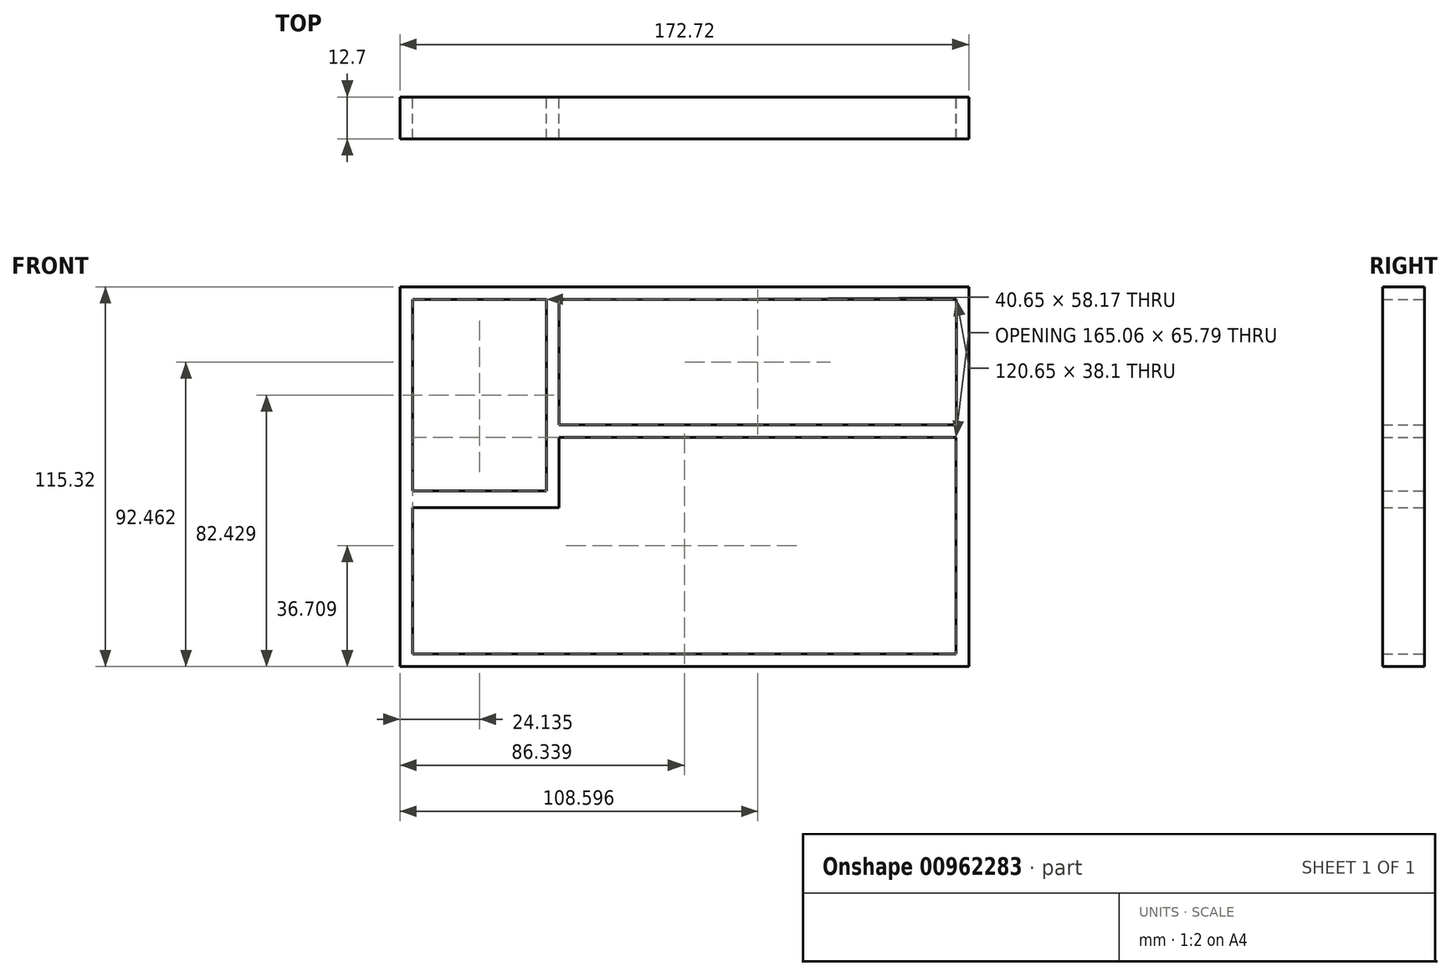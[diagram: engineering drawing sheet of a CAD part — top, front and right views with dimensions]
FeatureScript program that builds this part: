
annotation { "Feature Type Name" : "Feature", "Feature Type Description" : "" }
export const myFeature = defineFeature(function(context is Context, id is Id, definition is map)
    precondition{}
    {
        {
            var Q0;
            Q0=qCreatedBy(makeId("Front.planeOp"),FACE);
            var sketch = newSketch(context, id + "F0", { "sketchPlane" : qUnion([Q0])});
            skLineSegment(sketch, "E0.top", {"start": v(-81.04, -48) * mm, "end": v(84.02, -48) * mm});
            skLineSegment(sketch, "E0.left", {"start": v(-81.04, -3.56) * mm, "end": v(-81.04, -48) * mm});
            skLineSegment(sketch, "E0.right", {"start": v(84.02, -5.13) * mm, "end": v(84.02, -48) * mm});
            skLineSegment(sketch, "E1.top", {"start": v(-84.85, -51.82) * mm, "end": v(87.87, -51.82) * mm});
            skLineSegment(sketch, "E1.right", {"start": v(87.87, 17.78) * mm, "end": v(87.87, -51.82) * mm});
            skLineSegment(sketch, "E2.top", {"start": v(87.87, 63.5) * mm, "end": v(-84.85, 63.5) * mm});
            skLineSegment(sketch, "E2.left", {"start": v(87.87, 17.78) * mm, "end": v(87.87, 63.5) * mm});
            skLineSegment(sketch, "E3.left", {"start": v(-81.04, 1.52) * mm, "end": v(-81.04, 59.7) * mm});
            skLineSegment(sketch, "E3.right", {"start": v(84.07, 21.6) * mm, "end": v(84.07, 59.7) * mm});
            skPoint(sketch, "E4.endSnap0", {"position": v(1.51, 21.6) * mm});
            skLineSegment(sketch, "E5.left", {"start": v(-40.39, 59.7) * mm, "end": v(-40.39, 1.52) * mm});
            skLineSegment(sketch, "E5.right", {"start": v(-36.58, 59.7) * mm, "end": v(-36.58, 21.6) * mm});
            skLineSegment(sketch, "E6", {"start": v(-84.85, 63.5) * mm, "end": v(-84.85, -51.82) * mm});
            skLineSegment(sketch, "E7", {"start": v(-81.04, 1.52) * mm, "end": v(-40.39, 1.52) * mm});
            skLineSegment(sketch, "E8", {"start": v(-81.04, 59.7) * mm, "end": v(-40.39, 59.7) * mm});
            skLineSegment(sketch, "E9", {"start": v(-36.58, 59.7) * mm, "end": v(84.07, 59.7) * mm});
            skLineSegment(sketch, "E10", {"start": v(84.07, 21.6) * mm, "end": v(-36.58, 21.6) * mm});
            skLineSegment(sketch, "E11", {"start": v(-81.04, -3.56) * mm, "end": v(-40.39, -3.56) * mm});
            skLineSegment(sketch, "E12", {"start": v(-40.39, -3.56) * mm, "end": v(-36.58, -3.56) * mm});
            skLineSegment(sketch, "E13", {"start": v(-36.58, -3.56) * mm, "end": v(-36.58, 17.78) * mm});
            skLineSegment(sketch, "E14", {"start": v(-36.58, 17.78) * mm, "end": v(84.02, 17.78) * mm});
            skLineSegment(sketch, "E15", {"start": v(84.02, 17.78) * mm, "end": v(84.02, -5.13) * mm});
            skSolve(sketch);
        }
        {
            var Q0;
            Q0=makeQuery(id+"F0.imprint","IMPRINT",FACE,{"disambiguationData":[TD([[makeQuery(id+"F0.imprint","IMPRINT",EDGE,{"derivedFrom":sQuery(id+"F0.wireOp",EDGE,"E0.top")}),-1.0]])]});
            extrude(context, id + "F1", {"entities" : qUnion([Q0]), "depth" : 12.7 * mm, "offsetDistance" : 25.4 * mm});
        }
    });
